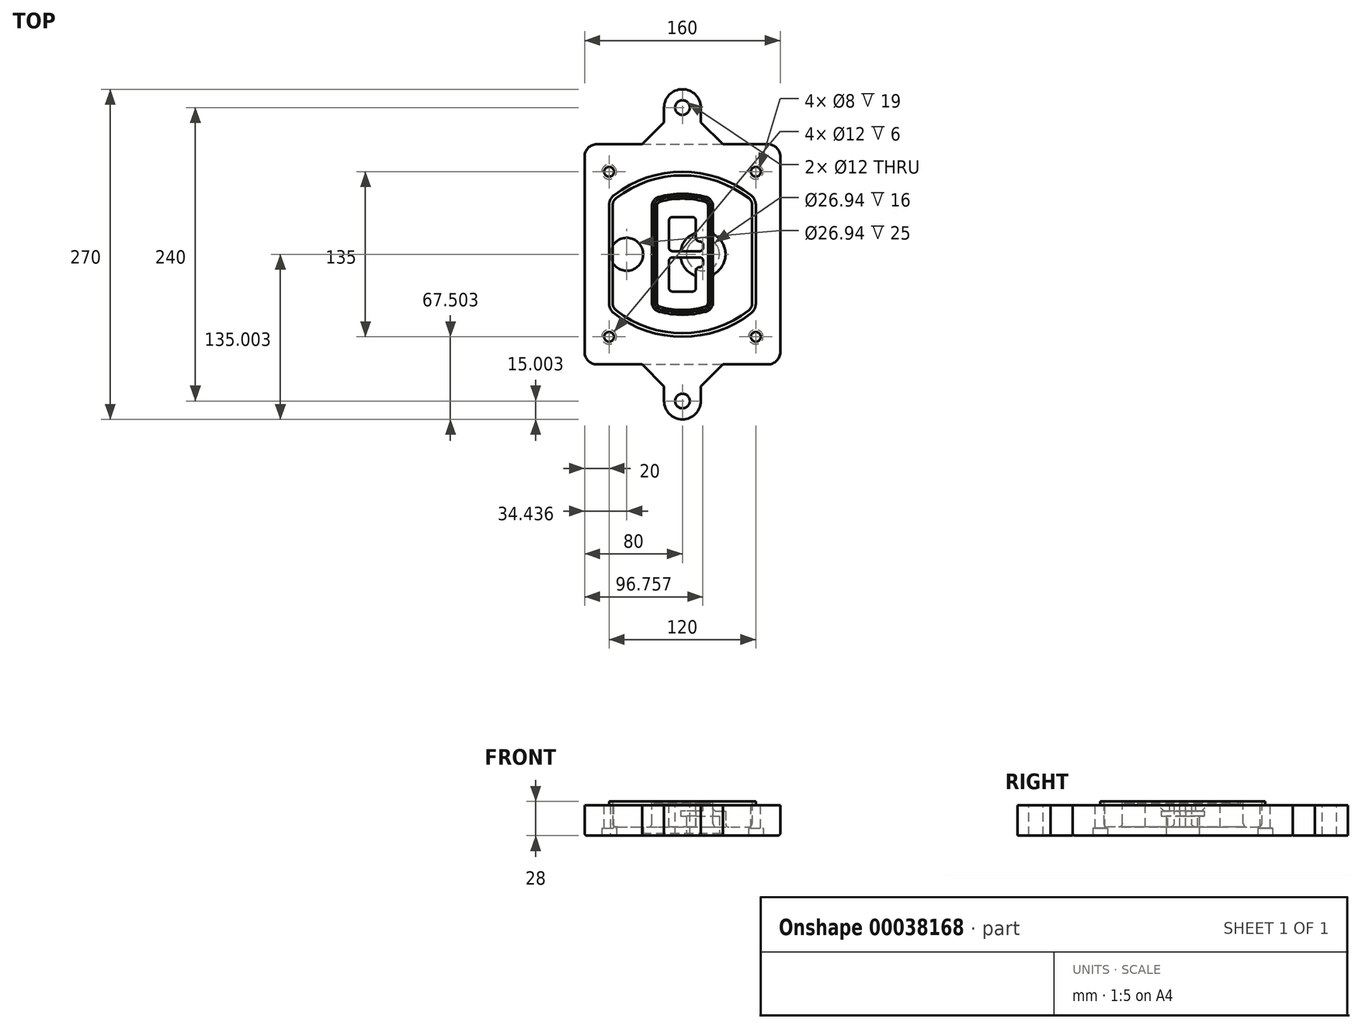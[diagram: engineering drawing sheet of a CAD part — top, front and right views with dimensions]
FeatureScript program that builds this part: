
annotation { "Feature Type Name" : "Feature", "Feature Type Description" : "" }
export const myFeature = defineFeature(function(context is Context, id is Id, definition is map)
    precondition{}
    {
        {
            var Q0;
            Q0=qCreatedBy(makeId("Top.planeOp"),FACE);
            var sketch = newSketch(context, id + "F0", { "sketchPlane" : qUnion([Q0])});
            skPoint(sketch, "E0.rect.middle", {"position": v(0, 0) * mm});
            skLineSegment(sketch, "E1.bottom", {"start": v(24.05, 28.38) * mm, "end": v(164.05, 28.38) * mm});
            skLineSegment(sketch, "E1.top", {"start": v(24.05, 208.38) * mm, "end": v(164.05, 208.38) * mm});
            skLineSegment(sketch, "E1.left", {"start": v(14.05, 38.38) * mm, "end": v(14.05, 198.38) * mm});
            skLineSegment(sketch, "E1.right", {"start": v(174.05, 38.38) * mm, "end": v(174.05, 198.38) * mm});
            skLineSegment(sketch, "E2", {"start": v(14.05, 208.38) * mm, "end": v(174.05, 28.38) * mm, "construction": true});
            skLineSegment(sketch, "E3", {"start": v(174.05, 208.38) * mm, "end": v(14.05, 28.38) * mm, "construction": true});
            skCircle(sketch, "E4", {"center": v(34.05, 185.88) * mm, "radius": 4 * mm});
            skCircle(sketch, "E5", {"center": v(154.05, 185.88) * mm, "radius": 4 * mm});
            skCircle(sketch, "E6", {"center": v(154.05, 50.88) * mm, "radius": 4 * mm});
            skCircle(sketch, "E7", {"center": v(34.05, 50.88) * mm, "radius": 4 * mm});
            skLineSegment(sketch, "E8", {"start": v(34.05, 185.88) * mm, "end": v(154.05, 185.88) * mm, "construction": true});
            skLineSegment(sketch, "E9", {"start": v(154.05, 185.88) * mm, "end": v(154.05, 50.88) * mm, "construction": true});
            skLineSegment(sketch, "E10", {"start": v(154.05, 50.88) * mm, "end": v(34.05, 50.88) * mm, "construction": true});
            skLineSegment(sketch, "E11", {"start": v(34.05, 50.88) * mm, "end": v(34.05, 185.88) * mm, "construction": true});
            skLineSegment(sketch, "E12", {"start": v(34.05, 158.68) * mm, "end": v(34.05, 78.09) * mm});
            skLineSegment(sketch, "E13", {"start": v(154.05, 158.68) * mm, "end": v(154.05, 78.09) * mm});
            skArc(sketch, "E14", {"start": v(150.2, 166.56) * mm, "mid": v(94.05, 185.88) * mm, "end": v(37.9, 166.56) * mm});
            skArc(sketch, "E15", {"start": v(37.9, 70.2) * mm, "mid": v(94.05, 50.88) * mm, "end": v(150.2, 70.2) * mm});
            skLineSegment(sketch, "E16", {"start": v(34.05, 118.38) * mm, "end": v(154.05, 118.38) * mm, "construction": true});
            skPoint(sketch, "E17.visualSharp", {"position": v(34.05, 73.38) * mm});
            skArc(sketch, "E17.filletArc", {"start": v(34.05, 78.09) * mm, "mid": v(35.06, 73.7) * mm, "end": v(37.9, 70.2) * mm});
            skPoint(sketch, "E18.visualSharp", {"position": v(34.05, 163.38) * mm});
            skArc(sketch, "E18.filletArc", {"start": v(37.9, 166.56) * mm, "mid": v(35.06, 163.06) * mm, "end": v(34.05, 158.68) * mm});
            skPoint(sketch, "E19.visualSharp", {"position": v(154.05, 163.38) * mm});
            skArc(sketch, "E19.filletArc", {"start": v(154.05, 158.68) * mm, "mid": v(153.04, 163.06) * mm, "end": v(150.2, 166.56) * mm});
            skPoint(sketch, "E20.visualSharp", {"position": v(154.05, 73.38) * mm});
            skArc(sketch, "E20.filletArc", {"start": v(150.2, 70.2) * mm, "mid": v(153.04, 73.7) * mm, "end": v(154.05, 78.09) * mm});
            skPoint(sketch, "E21.visualSharp", {"position": v(14.05, 208.38) * mm});
            skArc(sketch, "E21.filletArc", {"start": v(24.05, 208.38) * mm, "mid": v(16.98, 205.45) * mm, "end": v(14.05, 198.38) * mm});
            skPoint(sketch, "E22.visualSharp", {"position": v(174.05, 208.38) * mm});
            skArc(sketch, "E22.filletArc", {"start": v(174.05, 198.38) * mm, "mid": v(171.12, 205.45) * mm, "end": v(164.05, 208.38) * mm});
            skPoint(sketch, "E23.visualSharp", {"position": v(174.05, 28.38) * mm});
            skArc(sketch, "E23.filletArc", {"start": v(164.05, 28.38) * mm, "mid": v(171.12, 31.31) * mm, "end": v(174.05, 38.38) * mm});
            skPoint(sketch, "E24.visualSharp", {"position": v(14.05, 28.38) * mm});
            skArc(sketch, "E24.filletArc", {"start": v(14.05, 38.38) * mm, "mid": v(16.98, 31.31) * mm, "end": v(24.05, 28.38) * mm});
            skArc(sketch, "E25.0", {"start": v(151.05, 158.68) * mm, "mid": v(150.34, 161.75) * mm, "end": v(148.36, 164.2) * mm});
            skLineSegment(sketch, "E25.1", {"start": v(151.05, 158.68) * mm, "end": v(151.05, 78.09) * mm});
            skArc(sketch, "E25.2", {"start": v(148.36, 72.57) * mm, "mid": v(150.34, 75.02) * mm, "end": v(151.05, 78.09) * mm});
            skArc(sketch, "E25.3", {"start": v(39.74, 72.57) * mm, "mid": v(94.05, 53.88) * mm, "end": v(148.36, 72.57) * mm});
            skArc(sketch, "E25.4", {"start": v(37.05, 78.09) * mm, "mid": v(37.76, 75.02) * mm, "end": v(39.74, 72.57) * mm});
            skArc(sketch, "E25.5", {"start": v(148.36, 164.2) * mm, "mid": v(94.05, 182.88) * mm, "end": v(39.74, 164.2) * mm});
            skLineSegment(sketch, "E25.6", {"start": v(37.05, 158.68) * mm, "end": v(37.05, 78.09) * mm});
            skArc(sketch, "E25.7", {"start": v(39.74, 164.2) * mm, "mid": v(37.76, 161.75) * mm, "end": v(37.05, 158.68) * mm});
            skArc(sketch, "E26.0", {"start": v(35.43, 169.71) * mm, "mid": v(31.47, 164.82) * mm, "end": v(30.05, 158.68) * mm});
            skArc(sketch, "E26.1", {"start": v(152.67, 169.71) * mm, "mid": v(94.05, 189.88) * mm, "end": v(35.43, 169.71) * mm});
            skArc(sketch, "E26.2", {"start": v(158.05, 158.68) * mm, "mid": v(156.63, 164.82) * mm, "end": v(152.67, 169.71) * mm});
            skLineSegment(sketch, "E26.3", {"start": v(158.05, 158.68) * mm, "end": v(158.05, 78.09) * mm});
            skArc(sketch, "E26.4", {"start": v(152.67, 67.05) * mm, "mid": v(156.63, 71.95) * mm, "end": v(158.05, 78.09) * mm});
            skLineSegment(sketch, "E26.5", {"start": v(30.05, 158.68) * mm, "end": v(30.05, 78.09) * mm});
            skArc(sketch, "E26.6", {"start": v(35.43, 67.05) * mm, "mid": v(94.05, 46.88) * mm, "end": v(152.67, 67.05) * mm});
            skArc(sketch, "E26.7", {"start": v(30.05, 78.09) * mm, "mid": v(31.47, 71.95) * mm, "end": v(35.43, 67.05) * mm});
            skSolve(sketch);
        }
        {
            var Q0;
            Q0=makeQuery(id+"F0.imprint","IMPRINT",FACE,{"disambiguationData":[TD([[makeQuery(id+"F0.imprint","IMPRINT",EDGE,{"derivedFrom":sQuery(id+"F0.wireOp",EDGE,"E1.bottom")}),1.0]])]});
            var Q1;
            Q1=makeQuery(id+"F0.imprint","IMPRINT",FACE,{"disambiguationData":[TD([[makeQuery(id+"F0.imprint","IMPRINT",EDGE,{"derivedFrom":sQuery(id+"F0.wireOp",EDGE,"E12")}),1.0]])]});
            var Q2;
            Q2=makeQuery(id+"F0.imprint","IMPRINT",FACE,{"disambiguationData":[TD([[makeQuery(id+"F0.imprint","IMPRINT",EDGE,{"derivedFrom":sQuery(id+"F0.wireOp",EDGE,"E25.0")}),1.0]])]});
            var Q3;
            Q3=makeQuery(id+"F0.imprint","IMPRINT",FACE,{"disambiguationData":[TD([[makeQuery(id+"F0.imprint","IMPRINT",EDGE,{"derivedFrom":sQuery(id+"F0.wireOp",EDGE,"E12")}),-1.0]])]});
            extrude(context, id + "F1", {"entities" : qUnion([Q0, Q1, Q2, Q3]), "oppositeDirection" : true, "depth" : 25 * mm});
        }
        {
            var Q0;
            Q0=makeQuery(id+"F0.imprint","IMPRINT",FACE,{"disambiguationData":[TD([[makeQuery(id+"F0.imprint","IMPRINT",EDGE,{"derivedFrom":sQuery(id+"F0.wireOp",EDGE,"E12")}),1.0]])]});
            extrude(context, id + "F2", {"entities" : qUnion([Q0]), "operationType" : NewBodyOperationType.ADD, "depth" : 3 * mm});
        }
        {
            var Q0;
            Q0=makeQuery(id+"F0.imprint","IMPRINT",FACE,{"disambiguationData":[TD([[makeQuery(id+"F0.imprint","IMPRINT",EDGE,{"derivedFrom":sQuery(id+"F0.wireOp",EDGE,"E25.0")}),1.0]])]});
            extrude(context, id + "F3", {"entities" : qUnion([Q0]), "operationType" : NewBodyOperationType.REMOVE, "oppositeDirection" : true, "depth" : 18 * mm});
        }
        {
            var Q0;
            Q0=makeQuery(id+"F2.opExtrude","CAP_FACE",FACE,{"disambiguationData":[OSD([sQuery(id+"F0.wireOp",EDGE,"E12"),sQuery(id+"F0.wireOp",EDGE,"E13"),sQuery(id+"F0.wireOp",EDGE,"E14"),sQuery(id+"F0.wireOp",EDGE,"E15"),sQuery(id+"F0.wireOp",EDGE,"E17.filletArc"),sQuery(id+"F0.wireOp",EDGE,"E18.filletArc"),sQuery(id+"F0.wireOp",EDGE,"E19.filletArc"),sQuery(id+"F0.wireOp",EDGE,"E20.filletArc"),sQuery(id+"F0.wireOp",EDGE,"E25.0"),sQuery(id+"F0.wireOp",EDGE,"E25.1"),sQuery(id+"F0.wireOp",EDGE,"E25.2"),sQuery(id+"F0.wireOp",EDGE,"E25.3"),sQuery(id+"F0.wireOp",EDGE,"E25.4"),sQuery(id+"F0.wireOp",EDGE,"E25.5"),sQuery(id+"F0.wireOp",EDGE,"E25.6"),sQuery(id+"F0.wireOp",EDGE,"E25.7")])],"isStart":false});
            var sketch = newSketch(context, id + "F4", { "sketchPlane" : qUnion([Q0])});
            skArc(sketch, "E27.0", {"start": v(74.97, 71.41) * mm, "mid": v(94.05, 68.88) * mm, "end": v(113.13, 71.41) * mm});
            skArc(sketch, "E28.0", {"start": v(113.13, 165.35) * mm, "mid": v(94.05, 167.88) * mm, "end": v(74.97, 165.35) * mm});
            skLineSegment(sketch, "E29", {"start": v(69.05, 157.63) * mm, "end": v(69.05, 79.14) * mm});
            skLineSegment(sketch, "E30", {"start": v(119.05, 157.63) * mm, "end": v(119.05, 79.14) * mm});
            skLineSegment(sketch, "E31", {"start": v(69.05, 163.48) * mm, "end": v(119.05, 163.48) * mm, "construction": true});
            skLineSegment(sketch, "E32", {"start": v(69.05, 73.28) * mm, "end": v(119.05, 73.28) * mm, "construction": true});
            skPoint(sketch, "E33.visualSharp", {"position": v(69.05, 163.48) * mm});
            skArc(sketch, "E33.filletArc", {"start": v(74.97, 165.35) * mm, "mid": v(70.7, 162.5) * mm, "end": v(69.05, 157.63) * mm});
            skPoint(sketch, "E34.visualSharp", {"position": v(119.05, 163.48) * mm});
            skArc(sketch, "E34.filletArc", {"start": v(119.05, 157.63) * mm, "mid": v(117.4, 162.5) * mm, "end": v(113.13, 165.35) * mm});
            skPoint(sketch, "E35.visualSharp", {"position": v(119.05, 73.28) * mm});
            skArc(sketch, "E35.filletArc", {"start": v(113.13, 71.41) * mm, "mid": v(117.4, 74.27) * mm, "end": v(119.05, 79.14) * mm});
            skPoint(sketch, "E36.visualSharp", {"position": v(69.05, 73.28) * mm});
            skArc(sketch, "E36.filletArc", {"start": v(69.05, 79.14) * mm, "mid": v(70.7, 74.27) * mm, "end": v(74.97, 71.41) * mm});
            skArc(sketch, "E37.0", {"start": v(148.36, 164.2) * mm, "mid": v(94.05, 182.88) * mm, "end": v(39.74, 164.2) * mm});
            skArc(sketch, "E37.1", {"start": v(39.74, 164.2) * mm, "mid": v(37.76, 161.75) * mm, "end": v(37.05, 158.68) * mm});
            skLineSegment(sketch, "E37.2", {"start": v(37.05, 158.68) * mm, "end": v(37.05, 78.09) * mm});
            skArc(sketch, "E37.3", {"start": v(37.05, 78.09) * mm, "mid": v(37.76, 75.02) * mm, "end": v(39.74, 72.57) * mm});
            skArc(sketch, "E37.4", {"start": v(39.74, 72.57) * mm, "mid": v(94.05, 53.88) * mm, "end": v(148.36, 72.57) * mm});
            skArc(sketch, "E37.5", {"start": v(148.36, 72.57) * mm, "mid": v(150.34, 75.02) * mm, "end": v(151.05, 78.09) * mm});
            skLineSegment(sketch, "E37.6", {"start": v(151.05, 158.68) * mm, "end": v(151.05, 78.09) * mm});
            skArc(sketch, "E37.7", {"start": v(151.05, 158.68) * mm, "mid": v(150.34, 161.75) * mm, "end": v(148.36, 164.2) * mm});
            skLineSegment(sketch, "E38.0", {"start": v(117.05, 157.63) * mm, "end": v(117.05, 79.14) * mm});
            skArc(sketch, "E38.1", {"start": v(112.61, 73.34) * mm, "mid": v(115.81, 75.49) * mm, "end": v(117.05, 79.14) * mm});
            skArc(sketch, "E38.2", {"start": v(75.49, 73.34) * mm, "mid": v(94.05, 70.88) * mm, "end": v(112.61, 73.34) * mm});
            skArc(sketch, "E38.3", {"start": v(71.05, 79.14) * mm, "mid": v(72.29, 75.49) * mm, "end": v(75.49, 73.34) * mm});
            skLineSegment(sketch, "E38.4", {"start": v(71.05, 157.63) * mm, "end": v(71.05, 79.14) * mm});
            skArc(sketch, "E38.5", {"start": v(117.05, 157.63) * mm, "mid": v(115.81, 161.28) * mm, "end": v(112.61, 163.42) * mm});
            skArc(sketch, "E38.6", {"start": v(75.49, 163.42) * mm, "mid": v(72.29, 161.28) * mm, "end": v(71.05, 157.63) * mm});
            skArc(sketch, "E38.7", {"start": v(112.61, 163.42) * mm, "mid": v(94.05, 165.88) * mm, "end": v(75.49, 163.42) * mm});
            skArc(sketch, "E39.0", {"start": v(115.05, 157.63) * mm, "mid": v(114.23, 160.06) * mm, "end": v(112.1, 161.5) * mm});
            skLineSegment(sketch, "E39.1", {"start": v(115.05, 157.63) * mm, "end": v(115.05, 79.14) * mm});
            skArc(sketch, "E39.2", {"start": v(112.1, 75.27) * mm, "mid": v(114.23, 76.7) * mm, "end": v(115.05, 79.14) * mm});
            skArc(sketch, "E39.3", {"start": v(76, 75.27) * mm, "mid": v(94.05, 72.88) * mm, "end": v(112.1, 75.27) * mm});
            skArc(sketch, "E39.4", {"start": v(73.05, 79.14) * mm, "mid": v(73.87, 76.7) * mm, "end": v(76, 75.27) * mm});
            skArc(sketch, "E39.5", {"start": v(112.1, 161.5) * mm, "mid": v(94.05, 163.88) * mm, "end": v(76, 161.5) * mm});
            skLineSegment(sketch, "E39.6", {"start": v(73.05, 157.63) * mm, "end": v(73.05, 79.14) * mm});
            skArc(sketch, "E39.7", {"start": v(76, 161.5) * mm, "mid": v(73.87, 160.06) * mm, "end": v(73.05, 157.63) * mm});
            skLineSegment(sketch, "E40", {"start": v(69.05, 118.38) * mm, "end": v(119.05, 118.38) * mm, "construction": true});
            skLineSegment(sketch, "E41", {"start": v(83.05, 123.88) * mm, "end": v(83.05, 145.88) * mm});
            skLineSegment(sketch, "E42", {"start": v(86.05, 148.88) * mm, "end": v(102.05, 148.88) * mm});
            skLineSegment(sketch, "E43", {"start": v(105.05, 145.88) * mm, "end": v(105.05, 131.88) * mm});
            skLineSegment(sketch, "E44", {"start": v(108.05, 128.88) * mm, "end": v(108.05, 128.88) * mm});
            skLineSegment(sketch, "E45", {"start": v(111.05, 125.88) * mm, "end": v(111.05, 123.88) * mm});
            skLineSegment(sketch, "E46", {"start": v(108.05, 120.88) * mm, "end": v(86.05, 120.88) * mm});
            skPoint(sketch, "E47.visualSharp", {"position": v(83.05, 148.88) * mm});
            skArc(sketch, "E47.filletArc", {"start": v(86.05, 148.88) * mm, "mid": v(83.93, 148) * mm, "end": v(83.05, 145.88) * mm});
            skPoint(sketch, "E48.visualSharp", {"position": v(105.05, 148.88) * mm});
            skArc(sketch, "E48.filletArc", {"start": v(105.05, 145.88) * mm, "mid": v(104.17, 148) * mm, "end": v(102.05, 148.88) * mm});
            skPoint(sketch, "E49.visualSharp", {"position": v(105.05, 128.88) * mm});
            skArc(sketch, "E49.filletArc", {"start": v(105.05, 131.88) * mm, "mid": v(105.93, 129.76) * mm, "end": v(108.05, 128.88) * mm});
            skPoint(sketch, "E50.visualSharp", {"position": v(111.05, 128.88) * mm});
            skArc(sketch, "E50.filletArc", {"start": v(111.05, 125.88) * mm, "mid": v(110.17, 128) * mm, "end": v(108.05, 128.88) * mm});
            skPoint(sketch, "E51.visualSharp", {"position": v(111.05, 120.88) * mm});
            skArc(sketch, "E51.filletArc", {"start": v(108.05, 120.88) * mm, "mid": v(110.17, 121.76) * mm, "end": v(111.05, 123.88) * mm});
            skPoint(sketch, "E52.visualSharp", {"position": v(83.05, 120.88) * mm});
            skArc(sketch, "E52.filletArc", {"start": v(83.05, 123.88) * mm, "mid": v(83.93, 121.76) * mm, "end": v(86.05, 120.88) * mm});
            skLineSegment(sketch, "E53.0.MirrorCS", {"start": v(108.05, 115.88) * mm, "end": v(86.05, 115.88) * mm});
            skArc(sketch, "E54.0.MirrorCS", {"start": v(83.05, 112.88) * mm, "mid": v(83.93, 115) * mm, "end": v(86.05, 115.88) * mm});
            skLineSegment(sketch, "E55.0.MirrorCS", {"start": v(83.05, 112.88) * mm, "end": v(83.05, 90.88) * mm});
            skArc(sketch, "E56.0.MirrorCS", {"start": v(86.05, 87.88) * mm, "mid": v(83.93, 88.76) * mm, "end": v(83.05, 90.88) * mm});
            skLineSegment(sketch, "E57.0.MirrorCS", {"start": v(86.05, 87.88) * mm, "end": v(102.05, 87.88) * mm});
            skArc(sketch, "E58.0.MirrorCS", {"start": v(105.05, 90.88) * mm, "mid": v(104.17, 88.76) * mm, "end": v(102.05, 87.88) * mm});
            skLineSegment(sketch, "E59.0.MirrorCS", {"start": v(105.05, 90.88) * mm, "end": v(105.05, 104.88) * mm});
            skArc(sketch, "E60.0.MirrorCS", {"start": v(105.05, 104.88) * mm, "mid": v(105.93, 107) * mm, "end": v(108.05, 107.88) * mm});
            skArc(sketch, "E61.0.MirrorCS", {"start": v(111.05, 110.88) * mm, "mid": v(110.17, 108.76) * mm, "end": v(108.05, 107.88) * mm});
            skLineSegment(sketch, "E62.0.MirrorCS", {"start": v(111.05, 110.88) * mm, "end": v(111.05, 112.88) * mm});
            skArc(sketch, "E63.0.MirrorCS", {"start": v(108.05, 115.88) * mm, "mid": v(110.17, 115) * mm, "end": v(111.05, 112.88) * mm});
            skSolve(sketch);
        }
        {
            var Q0;
            Q0=makeQuery(id+"F4.imprint","IMPRINT",FACE,{"disambiguationData":[TD([[makeQuery(id+"F4.imprint","IMPRINT",EDGE,{"derivedFrom":sQuery(id+"F4.wireOp",EDGE,"E27.0")}),1.0]])]});
            var Q1;
            Q1=makeQuery(id+"F4.imprint","IMPRINT",FACE,{"disambiguationData":[TD([[makeQuery(id+"F4.imprint","IMPRINT",EDGE,{"derivedFrom":sQuery(id+"F4.wireOp",EDGE,"E38.0")}),-1.0]])]});
            var Q2;
            Q2=makeQuery(id+"F4.imprint","IMPRINT",FACE,{"disambiguationData":[TD([[makeQuery(id+"F4.imprint","IMPRINT",EDGE,{"derivedFrom":sQuery(id+"F4.wireOp",EDGE,"E39.0")}),1.0]])]});
            extrude(context, id + "F5", {"entities" : qUnion([Q0, Q1, Q2]), "operationType" : NewBodyOperationType.ADD, "endBound" : BoundingType.UP_TO_NEXT, "oppositeDirection" : true, "depth" : 25 * mm});
        }
        {
            var Q0;
            Q0=makeQuery(id+"F4.imprint","IMPRINT",FACE,{"disambiguationData":[TD([[makeQuery(id+"F4.imprint","IMPRINT",EDGE,{"derivedFrom":sQuery(id+"F4.wireOp",EDGE,"E38.0")}),-1.0]])]});
            extrude(context, id + "F6", {"entities" : qUnion([Q0]), "operationType" : NewBodyOperationType.REMOVE, "oppositeDirection" : true, "depth" : 2 * mm});
        }
        {
            var Q0;
            Q0=makeQuery(id+"F1.opExtrude","CAP_FACE",FACE,{"disambiguationData":[OSD([sQuery(id+"F0.wireOp",EDGE,"E1.bottom"),sQuery(id+"F0.wireOp",EDGE,"E1.top"),sQuery(id+"F0.wireOp",EDGE,"E1.left"),sQuery(id+"F0.wireOp",EDGE,"E1.right"),sQuery(id+"F0.wireOp",EDGE,"E4"),sQuery(id+"F0.wireOp",EDGE,"E5"),sQuery(id+"F0.wireOp",EDGE,"E6"),sQuery(id+"F0.wireOp",EDGE,"E7"),sQuery(id+"F0.wireOp",EDGE,"E21.filletArc"),sQuery(id+"F0.wireOp",EDGE,"E22.filletArc"),sQuery(id+"F0.wireOp",EDGE,"E23.filletArc"),sQuery(id+"F0.wireOp",EDGE,"E24.filletArc")])],"isStart":false});
            var sketch = newSketch(context, id + "F7", { "sketchPlane" : qUnion([Q0])});
            skCircle(sketch, "E64", {"center": v(110.8, -118.38) * mm, "radius": 13.47 * mm});
            skCircle(sketch, "E65", {"center": v(48.49, -118.38) * mm, "radius": 13.47 * mm});
            skLineSegment(sketch, "E66", {"start": v(174.05, -118.38) * mm, "end": v(14.05, -118.38) * mm});
            skCircle(sketch, "E67", {"center": v(110.8, -118.38) * mm, "radius": 18.47 * mm});
            skCircle(sketch, "E68", {"center": v(154.05, -185.88) * mm, "radius": 6 * mm});
            skCircle(sketch, "E69", {"center": v(34.05, -185.88) * mm, "radius": 6 * mm});
            skCircle(sketch, "E70", {"center": v(34.05, -50.88) * mm, "radius": 6 * mm});
            skCircle(sketch, "E71", {"center": v(154.05, -50.88) * mm, "radius": 6 * mm});
            skSolve(sketch);
        }
        {
            var Q0;
            {var subQ1=sQuery(id+"F7.wireOp",EDGE,"E66");var subQ4=sQuery(id+"F7.wireOp",EDGE,"E64");var subQ6=makeQuery(id+"F7.imprint","INTERSECT",VERTEX,{"disambiguationData":[OD(0.0)],"derivedFrom":[subQ4,subQ1]});Q0=makeQuery(id+"F7.imprint","IMPRINT",FACE,{"disambiguationData":[TD([[makeQuery(id+"F7.imprint","IMPRINT",EDGE,{"disambiguationData":[TD([[subQ6,-1.0]])],"derivedFrom":subQ4}),-1.0]])]});}
            var Q1;
            {var subQ0=sQuery(id+"F7.wireOp",EDGE,"E66");var subQ1=sQuery(id+"F7.wireOp",EDGE,"E64");var subQ3=makeQuery(id+"F7.imprint","INTERSECT",VERTEX,{"disambiguationData":[OD(0.0)],"derivedFrom":[subQ1,subQ0]});Q1=makeQuery(id+"F7.imprint","IMPRINT",FACE,{"disambiguationData":[TD([[makeQuery(id+"F7.imprint","IMPRINT",EDGE,{"disambiguationData":[TD([[subQ3,-1.0]])],"derivedFrom":subQ1}),1.0]])]});}
            var Q2;
            {var subQ0=sQuery(id+"F7.wireOp",EDGE,"E66");var subQ1=sQuery(id+"F7.wireOp",EDGE,"E64");var subQ3=makeQuery(id+"F7.imprint","INTERSECT",VERTEX,{"disambiguationData":[OD(0.0)],"derivedFrom":[subQ1,subQ0]});Q2=makeQuery(id+"F7.imprint","IMPRINT",FACE,{"disambiguationData":[TD([[makeQuery(id+"F7.imprint","IMPRINT",EDGE,{"disambiguationData":[TD([[subQ3,1.0]])],"derivedFrom":subQ1}),1.0]])]});}
            var Q3;
            {var subQ1=sQuery(id+"F7.wireOp",EDGE,"E66");var subQ4=sQuery(id+"F7.wireOp",EDGE,"E64");var subQ6=makeQuery(id+"F7.imprint","INTERSECT",VERTEX,{"disambiguationData":[OD(0.0)],"derivedFrom":[subQ4,subQ1]});Q3=makeQuery(id+"F7.imprint","IMPRINT",FACE,{"disambiguationData":[TD([[makeQuery(id+"F7.imprint","IMPRINT",EDGE,{"disambiguationData":[TD([[subQ6,1.0]])],"derivedFrom":subQ4}),-1.0]])]});}
            extrude(context, id + "F8", {"entities" : qUnion([Q0, Q1, Q2, Q3]), "operationType" : NewBodyOperationType.ADD, "oppositeDirection" : true, "depth" : 20 * mm});
        }
        {
            var Q0;
            {var subQ0=sQuery(id+"F7.wireOp",EDGE,"E66");var subQ1=sQuery(id+"F7.wireOp",EDGE,"E64");var subQ3=makeQuery(id+"F7.imprint","INTERSECT",VERTEX,{"disambiguationData":[OD(0.0)],"derivedFrom":[subQ1,subQ0]});Q0=makeQuery(id+"F7.imprint","IMPRINT",FACE,{"disambiguationData":[TD([[makeQuery(id+"F7.imprint","IMPRINT",EDGE,{"disambiguationData":[TD([[subQ3,-1.0]])],"derivedFrom":subQ1}),1.0]])]});}
            var Q1;
            {var subQ0=sQuery(id+"F7.wireOp",EDGE,"E66");var subQ1=sQuery(id+"F7.wireOp",EDGE,"E64");var subQ3=makeQuery(id+"F7.imprint","INTERSECT",VERTEX,{"disambiguationData":[OD(0.0)],"derivedFrom":[subQ1,subQ0]});Q1=makeQuery(id+"F7.imprint","IMPRINT",FACE,{"disambiguationData":[TD([[makeQuery(id+"F7.imprint","IMPRINT",EDGE,{"disambiguationData":[TD([[subQ3,1.0]])],"derivedFrom":subQ1}),1.0]])]});}
            extrude(context, id + "F9", {"entities" : qUnion([Q0, Q1]), "operationType" : NewBodyOperationType.REMOVE, "oppositeDirection" : true, "depth" : 16 * mm});
        }
        {
            var Q0;
            {var subQ0=sQuery(id+"F7.wireOp",EDGE,"E66");var subQ1=sQuery(id+"F7.wireOp",EDGE,"E65");var subQ3=makeQuery(id+"F7.imprint","INTERSECT",VERTEX,{"disambiguationData":[OD(0.0)],"derivedFrom":[subQ1,subQ0]});Q0=makeQuery(id+"F7.imprint","IMPRINT",FACE,{"disambiguationData":[TD([[makeQuery(id+"F7.imprint","IMPRINT",EDGE,{"disambiguationData":[TD([[subQ3,-1.0]])],"derivedFrom":subQ1}),1.0]])]});}
            var Q1;
            {var subQ0=sQuery(id+"F7.wireOp",EDGE,"E66");var subQ1=sQuery(id+"F7.wireOp",EDGE,"E65");var subQ3=makeQuery(id+"F7.imprint","INTERSECT",VERTEX,{"disambiguationData":[OD(0.0)],"derivedFrom":[subQ1,subQ0]});Q1=makeQuery(id+"F7.imprint","IMPRINT",FACE,{"disambiguationData":[TD([[makeQuery(id+"F7.imprint","IMPRINT",EDGE,{"disambiguationData":[TD([[subQ3,1.0]])],"derivedFrom":subQ1}),1.0]])]});}
            extrude(context, id + "F10", {"entities" : qUnion([Q0, Q1]), "operationType" : NewBodyOperationType.REMOVE, "oppositeDirection" : true, "depth" : 25 * mm});
        }
        {
            var Q0;
            Q0=makeQuery(id+"F7.imprint","IMPRINT",FACE,{"disambiguationData":[TD([[makeQuery(id+"F7.imprint","IMPRINT",EDGE,{"derivedFrom":sQuery(id+"F7.wireOp",EDGE,"E68")}),1.0]])]});
            var Q1;
            Q1=makeQuery(id+"F7.imprint","IMPRINT",FACE,{"disambiguationData":[TD([[makeQuery(id+"F7.imprint","IMPRINT",EDGE,{"derivedFrom":makeQuery(id+"F1.opExtrude","CAP_EDGE",EDGE,{"disambiguationData":[OSD([sQuery(id+"F0.wireOp",EDGE,"E5")])],"isStart":false})}),-1.0]])]});
            var Q2;
            Q2=makeQuery(id+"F7.imprint","IMPRINT",FACE,{"disambiguationData":[TD([[makeQuery(id+"F7.imprint","IMPRINT",EDGE,{"derivedFrom":sQuery(id+"F7.wireOp",EDGE,"E69")}),1.0]])]});
            var Q3;
            Q3=makeQuery(id+"F7.imprint","IMPRINT",FACE,{"disambiguationData":[TD([[makeQuery(id+"F7.imprint","IMPRINT",EDGE,{"derivedFrom":makeQuery(id+"F1.opExtrude","CAP_EDGE",EDGE,{"disambiguationData":[OSD([sQuery(id+"F0.wireOp",EDGE,"E4")])],"isStart":false})}),-1.0]])]});
            var Q4;
            Q4=makeQuery(id+"F7.imprint","IMPRINT",FACE,{"disambiguationData":[TD([[makeQuery(id+"F7.imprint","IMPRINT",EDGE,{"derivedFrom":sQuery(id+"F7.wireOp",EDGE,"E70")}),1.0]])]});
            var Q5;
            Q5=makeQuery(id+"F7.imprint","IMPRINT",FACE,{"disambiguationData":[TD([[makeQuery(id+"F7.imprint","IMPRINT",EDGE,{"derivedFrom":makeQuery(id+"F1.opExtrude","CAP_EDGE",EDGE,{"disambiguationData":[OSD([sQuery(id+"F0.wireOp",EDGE,"E7")])],"isStart":false})}),-1.0]])]});
            var Q6;
            Q6=makeQuery(id+"F7.imprint","IMPRINT",FACE,{"disambiguationData":[TD([[makeQuery(id+"F7.imprint","IMPRINT",EDGE,{"derivedFrom":sQuery(id+"F7.wireOp",EDGE,"E71")}),1.0]])]});
            var Q7;
            Q7=makeQuery(id+"F7.imprint","IMPRINT",FACE,{"disambiguationData":[TD([[makeQuery(id+"F7.imprint","IMPRINT",EDGE,{"derivedFrom":makeQuery(id+"F1.opExtrude","CAP_EDGE",EDGE,{"disambiguationData":[OSD([sQuery(id+"F0.wireOp",EDGE,"E6")])],"isStart":false})}),-1.0]])]});
            extrude(context, id + "F11", {"entities" : qUnion([Q0, Q1, Q2, Q3, Q4, Q5, Q6, Q7]), "operationType" : NewBodyOperationType.REMOVE, "oppositeDirection" : true, "depth" : 6 * mm});
        }
        {
            var Q0;
            Q0=makeQuery(id+"F9.boolean.opBoolean","COPY",FACE,{"derivedFrom":makeQuery(id+"F9.opExtrude","CAP_FACE",FACE,{"disambiguationData":[OSD([sQuery(id+"F7.wireOp",EDGE,"E64")])],"isStart":false})});
            var sketch = newSketch(context, id + "F12", { "sketchPlane" : qUnion([Q0])});
            skArc(sketch, "E72.0", {"start": v(105.05, -100.83) * mm, "mid": v(96.62, -106.56) * mm, "end": v(92.5, -115.88) * mm});
            skArc(sketch, "E72.1", {"start": v(92.5, -120.88) * mm, "mid": v(96.62, -130.2) * mm, "end": v(105.05, -135.93) * mm});
            skLineSegment(sketch, "E73", {"start": v(92.5, -120.88) * mm, "end": v(108.05, -120.88) * mm});
            skLineSegment(sketch, "E74.0", {"start": v(108.05, -115.88) * mm, "end": v(92.5, -115.88) * mm});
            skArc(sketch, "E74.1", {"start": v(108.05, -115.88) * mm, "mid": v(110.17, -115) * mm, "end": v(111.05, -112.88) * mm});
            skLineSegment(sketch, "E74.2", {"start": v(111.05, -110.88) * mm, "end": v(111.05, -112.88) * mm});
            skArc(sketch, "E74.3", {"start": v(111.05, -110.88) * mm, "mid": v(110.17, -108.76) * mm, "end": v(108.05, -107.88) * mm});
            skArc(sketch, "E74.4", {"start": v(105.05, -104.88) * mm, "mid": v(105.93, -107) * mm, "end": v(108.05, -107.88) * mm});
            skLineSegment(sketch, "E74.5", {"start": v(105.05, -100.83) * mm, "end": v(105.05, -104.88) * mm});
            skLineSegment(sketch, "E74.7", {"start": v(108.05, -120.88) * mm, "end": v(92.5, -120.88) * mm});
            skArc(sketch, "E74.8", {"start": v(108.05, -120.88) * mm, "mid": v(110.17, -121.76) * mm, "end": v(111.05, -123.88) * mm});
            skLineSegment(sketch, "E74.9", {"start": v(111.05, -125.88) * mm, "end": v(111.05, -123.88) * mm});
            skArc(sketch, "E74.10", {"start": v(111.05, -125.88) * mm, "mid": v(110.17, -128) * mm, "end": v(108.05, -128.88) * mm});
            skArc(sketch, "E74.11", {"start": v(105.05, -131.88) * mm, "mid": v(105.93, -129.76) * mm, "end": v(108.05, -128.88) * mm});
            skLineSegment(sketch, "E74.12", {"start": v(105.05, -135.93) * mm, "end": v(105.05, -131.88) * mm});
            skPoint(sketch, "E75.orphan", {"position": v(105.05, -145.88) * mm});
            skPoint(sketch, "E76.orphan", {"position": v(86.05, -120.88) * mm});
            skPoint(sketch, "E77.orphan", {"position": v(86.05, -115.88) * mm});
            skPoint(sketch, "E78.orphan", {"position": v(105.05, -90.88) * mm});
            skSolve(sketch);
        }
        {
            var Q0;
            {var subQ7=sQuery(id+"F12.wireOp",EDGE,"E72.0");var subQ14=sQuery(id+"F12.wireOp",EDGE,"E72.1");var subQ16=sQuery(id+"F12.wireOp",EDGE,"E74.1");var subQ18=sQuery(id+"F12.wireOp",EDGE,"E74.8");Q0=qUnion([makeQuery(id+"F12.imprint","IMPRINT",FACE,{"disambiguationData":[TD([[makeQuery(id+"F12.imprint","IMPRINT",EDGE,{"derivedFrom":subQ7}),1.0]])]}),makeQuery(id+"F12.imprint","IMPRINT",FACE,{"disambiguationData":[TD([[makeQuery(id+"F12.imprint","IMPRINT",EDGE,{"derivedFrom":subQ14}),1.0]])]}),makeQuery(id+"F12.imprint","IMPRINT",FACE,{"disambiguationData":[TD([[makeQuery(id+"F12.imprint","IMPRINT",EDGE,{"derivedFrom":subQ16}),1.0]])]}),makeQuery(id+"F12.imprint","IMPRINT",FACE,{"disambiguationData":[TD([[makeQuery(id+"F12.imprint","IMPRINT",EDGE,{"derivedFrom":subQ18}),-1.0]])]})]);}
            var Q1;
            Q1=makeQuery(id+"F5.boolean.opBoolean","SPLIT",FACE,{"disambiguationData":[TD([makeQuery(id+"F5.opExtrude","SWEPT_FACE",FACE,{"disambiguationData":[OSD([sQuery(id+"F4.wireOp",EDGE,"E41")])]})])],"derivedFrom":makeQuery(id+"F3.boolean.opBoolean","COPY",FACE,{"derivedFrom":makeQuery(id+"F3.opExtrude","CAP_FACE",FACE,{"disambiguationData":[OSD([sQuery(id+"F0.wireOp",EDGE,"E25.0"),sQuery(id+"F0.wireOp",EDGE,"E25.1"),sQuery(id+"F0.wireOp",EDGE,"E25.2"),sQuery(id+"F0.wireOp",EDGE,"E25.3"),sQuery(id+"F0.wireOp",EDGE,"E25.4"),sQuery(id+"F0.wireOp",EDGE,"E25.5"),sQuery(id+"F0.wireOp",EDGE,"E25.6"),sQuery(id+"F0.wireOp",EDGE,"E25.7")])],"isStart":false})})});
            extrude(context, id + "F13", {"entities" : qUnion([Q0]), "operationType" : NewBodyOperationType.REMOVE, "endBound" : BoundingType.UP_TO_SURFACE, "endBoundEntityFace" : qUnion([Q1]), "depth" : 25 * mm});
        }
        {
            var Q0;
            Q0=makeQuery(id+"F3.boolean.opBoolean","COPY",EDGE,{"derivedFrom":makeQuery(id+"F3.opExtrude","CAP_EDGE",EDGE,{"disambiguationData":[OSD([sQuery(id+"F0.wireOp",EDGE,"E25.6")])],"isStart":false})});
            var Q1;
            Q1=makeQuery(id+"F8.boolean.opBoolean","INTERSECT",EDGE,{"derivedFrom":[makeQuery(id+"F5.opExtrude","SWEPT_FACE",FACE,{"disambiguationData":[OSD([sQuery(id+"F4.wireOp",EDGE,"E30")])]}),makeQuery(id+"F8.opExtrude","CAP_FACE",FACE,{"disambiguationData":[OSD([sQuery(id+"F7.wireOp",EDGE,"E67")])],"isStart":false})]});
            var Q2;
            Q2=makeQuery(id+"F8.boolean.opBoolean","INTERSECT",EDGE,{"disambiguationData":[OD(1.0)],"derivedFrom":[makeQuery(id+"F5.opExtrude","SWEPT_FACE",FACE,{"disambiguationData":[OSD([sQuery(id+"F4.wireOp",EDGE,"E30")])]}),makeQuery(id+"F8.opExtrude","SWEPT_FACE",FACE,{"disambiguationData":[OSD([sQuery(id+"F7.wireOp",EDGE,"E67")])]})]});
            var Q3;
            {var subQ0=sQuery(id+"F4.wireOp",EDGE,"E30");Q3=makeQuery(id+"F8.boolean.opBoolean","SPLIT",EDGE,{"disambiguationData":[TD([makeQuery(id+"F5.opExtrude","SWEPT_FACE",FACE,{"disambiguationData":[OSD([sQuery(id+"F4.wireOp",EDGE,"E35.filletArc")])]})])],"derivedFrom":makeQuery(id+"F5.opExtrude","CAP_EDGE",EDGE,{"disambiguationData":[OSD([subQ0])],"isStart":false})});}
            var Q4;
            {var subQ0=sQuery(id+"F0.wireOp",EDGE,"E25.7");var subQ1=sQuery(id+"F0.wireOp",EDGE,"E25.1");var subQ2=sQuery(id+"F0.wireOp",EDGE,"E25.6");var subQ3=sQuery(id+"F0.wireOp",EDGE,"E25.5");var subQ4=sQuery(id+"F0.wireOp",EDGE,"E25.4");var subQ5=sQuery(id+"F0.wireOp",EDGE,"E25.0");var subQ6=sQuery(id+"F0.wireOp",EDGE,"E25.2");var subQ7=sQuery(id+"F0.wireOp",EDGE,"E25.3");Q4=makeQuery(id+"F8.boolean.opBoolean","INTERSECT",EDGE,{"derivedFrom":[makeQuery(id+"F5.boolean.opBoolean","SPLIT",FACE,{"disambiguationData":[TD([makeQuery(id+"F2.opExtrude","SWEPT_FACE",FACE,{"disambiguationData":[OSD([subQ5])]})])],"derivedFrom":makeQuery(id+"F3.boolean.opBoolean","COPY",FACE,{"derivedFrom":makeQuery(id+"F3.opExtrude","CAP_FACE",FACE,{"disambiguationData":[OSD([subQ5,subQ1,subQ6,subQ7,subQ4,subQ3,subQ2,subQ0])],"isStart":false})})}),makeQuery(id+"F8.opExtrude","SWEPT_FACE",FACE,{"disambiguationData":[OSD([sQuery(id+"F7.wireOp",EDGE,"E67")])]})]});}
            var Q5;
            Q5=makeQuery(id+"F8.boolean.opBoolean","INTERSECT",EDGE,{"disambiguationData":[OD(0.0)],"derivedFrom":[makeQuery(id+"F5.opExtrude","SWEPT_FACE",FACE,{"disambiguationData":[OSD([sQuery(id+"F4.wireOp",EDGE,"E30")])]}),makeQuery(id+"F8.opExtrude","SWEPT_FACE",FACE,{"disambiguationData":[OSD([sQuery(id+"F7.wireOp",EDGE,"E67")])]})]});
            fillet(context, id + "F14", {"entities" : qUnion([Q0, Q1, Q2, Q3, Q4, Q5]), "radius" : 3 * mm, "tangentPropagation" : true, "allowEdgeOverflow" : false});
        }
        {
            var Q0;
            Q0=makeQuery(id+"F1.opExtrude","CAP_EDGE",EDGE,{"disambiguationData":[OSD([sQuery(id+"F0.wireOp",EDGE,"E1.bottom")])],"isStart":false});
            fillet(context, id + "F15", {"entities" : qUnion([Q0]), "radius" : 2 * mm, "tangentPropagation" : true, "allowEdgeOverflow" : false});
        }
        {
            var Q0;
            {var subQ0=sQuery(id+"F0.wireOp",EDGE,"E1.bottom");var subQ1=sQuery(id+"F0.wireOp",EDGE,"E1.top");var subQ2=sQuery(id+"F0.wireOp",EDGE,"E1.left");var subQ3=sQuery(id+"F0.wireOp",EDGE,"E1.right");var subQ4=sQuery(id+"F0.wireOp",EDGE,"E4");var subQ5=sQuery(id+"F0.wireOp",EDGE,"E5");var subQ6=sQuery(id+"F0.wireOp",EDGE,"E6");var subQ7=sQuery(id+"F0.wireOp",EDGE,"E7");var subQ8=sQuery(id+"F0.wireOp",EDGE,"E21.filletArc");var subQ9=sQuery(id+"F0.wireOp",EDGE,"E22.filletArc");var subQ10=sQuery(id+"F0.wireOp",EDGE,"E23.filletArc");var subQ11=sQuery(id+"F0.wireOp",EDGE,"E24.filletArc");Q0=makeQuery(id+"F2.boolean.opBoolean","SPLIT",FACE,{"disambiguationData":[TD([makeQuery(id+"F1.opExtrude","SWEPT_FACE",FACE,{"disambiguationData":[OSD([subQ0])]})])],"derivedFrom":makeQuery(id+"F1.opExtrude","CAP_FACE",FACE,{"disambiguationData":[OSD([subQ0,subQ1,subQ2,subQ3,subQ4,subQ5,subQ6,subQ7,subQ8,subQ9,subQ10,subQ11])],"isStart":true})});}
            var sketch = newSketch(context, id + "F16", { "sketchPlane" : qUnion([Q0])});
            skArc(sketch, "E79.0", {"start": v(37.9, 166.56) * mm, "mid": v(35.06, 163.06) * mm, "end": v(34.05, 158.68) * mm});
            skLineSegment(sketch, "E79.1", {"start": v(34.05, 158.68) * mm, "end": v(34.05, 78.09) * mm});
            skArc(sketch, "E79.2", {"start": v(150.2, 166.56) * mm, "mid": v(94.05, 185.88) * mm, "end": v(37.9, 166.56) * mm});
            skArc(sketch, "E79.3", {"start": v(154.05, 158.68) * mm, "mid": v(153.04, 163.06) * mm, "end": v(150.2, 166.56) * mm});
            skLineSegment(sketch, "E79.4", {"start": v(154.05, 158.68) * mm, "end": v(154.05, 78.09) * mm});
            skArc(sketch, "E79.5", {"start": v(150.2, 70.2) * mm, "mid": v(153.04, 73.7) * mm, "end": v(154.05, 78.09) * mm});
            skArc(sketch, "E79.6", {"start": v(37.9, 70.2) * mm, "mid": v(94.05, 50.88) * mm, "end": v(150.2, 70.2) * mm});
            skArc(sketch, "E79.7", {"start": v(34.05, 78.09) * mm, "mid": v(35.06, 73.7) * mm, "end": v(37.9, 70.2) * mm});
            skCircle(sketch, "E79.8", {"center": v(34.05, 50.88) * mm, "radius": 4 * mm});
            skCircle(sketch, "E79.9", {"center": v(154.05, 185.88) * mm, "radius": 4 * mm});
            skCircle(sketch, "E79.10", {"center": v(154.05, 50.88) * mm, "radius": 4 * mm});
            skCircle(sketch, "E79.11", {"center": v(34.05, 185.88) * mm, "radius": 4 * mm});
            skArc(sketch, "E80.12", {"start": v(24.05, 208.38) * mm, "mid": v(16.98, 205.45) * mm, "end": v(14.05, 198.38) * mm});
            skLineSegment(sketch, "E80.13", {"start": v(14.05, 38.38) * mm, "end": v(14.05, 198.38) * mm});
            skLineSegment(sketch, "E80.14", {"start": v(24.05, 28.38) * mm, "end": v(164.05, 28.38) * mm});
            skArc(sketch, "E80.15", {"start": v(14.05, 38.38) * mm, "mid": v(16.98, 31.31) * mm, "end": v(24.05, 28.38) * mm});
            skArc(sketch, "E80.16", {"start": v(164.05, 28.38) * mm, "mid": v(171.12, 31.31) * mm, "end": v(174.05, 38.38) * mm});
            skLineSegment(sketch, "E80.17", {"start": v(174.05, 38.38) * mm, "end": v(174.05, 198.38) * mm});
            skArc(sketch, "E80.18", {"start": v(174.05, 198.38) * mm, "mid": v(171.12, 205.45) * mm, "end": v(164.05, 208.38) * mm});
            skLineSegment(sketch, "E80.19", {"start": v(24.05, 208.38) * mm, "end": v(164.05, 208.38) * mm});
            skCircle(sketch, "E81", {"center": v(94.05, 238.38) * mm, "radius": 6 * mm});
            skArc(sketch, "E82", {"start": v(109.05, 238.38) * mm, "mid": v(94.05, 253.38) * mm, "end": v(79.05, 238.38) * mm});
            skLineSegment(sketch, "E83", {"start": v(79.05, 238.38) * mm, "end": v(79.05, 226.38) * mm});
            skLineSegment(sketch, "E84", {"start": v(79.05, 226.38) * mm, "end": v(61.05, 208.38) * mm});
            skLineSegment(sketch, "E85", {"start": v(109.05, 238.38) * mm, "end": v(109.05, 226.38) * mm});
            skLineSegment(sketch, "E86", {"start": v(109.05, 226.38) * mm, "end": v(127.05, 208.38) * mm});
            skLineSegment(sketch, "E87", {"start": v(94.05, 238.38) * mm, "end": v(94.05, 208.38) * mm, "construction": true});
            skArc(sketch, "E88.MirrorCS", {"start": v(79.05, 238.38) * mm, "mid": v(94.05, 253.38) * mm, "end": v(109.05, 238.38) * mm});
            skLineSegment(sketch, "E89", {"start": v(174.05, 118.38) * mm, "end": v(14.05, 118.38) * mm, "construction": true});
            skLineSegment(sketch, "E90.MirrorCS", {"start": v(109.05, 10.38) * mm, "end": v(127.05, 28.38) * mm});
            skLineSegment(sketch, "E91.MirrorCS", {"start": v(79.05, 10.38) * mm, "end": v(61.05, 28.38) * mm});
            skLineSegment(sketch, "E92.MirrorCS", {"start": v(79.05, -1.62) * mm, "end": v(79.05, 10.38) * mm});
            skArc(sketch, "E93.MirrorCS", {"start": v(109.05, -1.62) * mm, "mid": v(94.05, -16.62) * mm, "end": v(79.05, -1.62) * mm});
            skLineSegment(sketch, "E94.MirrorCS", {"start": v(109.05, -1.62) * mm, "end": v(109.05, 10.38) * mm});
            skCircle(sketch, "E95.MirrorC", {"center": v(94.05, -1.62) * mm, "radius": 6 * mm});
            skLineSegment(sketch, "E96.MirrorCS", {"start": v(94.05, -1.62) * mm, "end": v(94.05, 28.38) * mm});
            skSolve(sketch);
        }
        {
            var Q0;
            {var subQ2=sQuery(id+"F16.wireOp",EDGE,"E84");Q0=makeQuery(id+"F16.imprint","IMPRINT",FACE,{"disambiguationData":[TD([[makeQuery(id+"F16.imprint","IMPRINT",EDGE,{"derivedFrom":subQ2}),1.0]])]});}
            var Q1;
            {var subQ3=sQuery(id+"F16.wireOp",EDGE,"E90.MirrorCS");Q1=makeQuery(id+"F16.imprint","IMPRINT",FACE,{"disambiguationData":[TD([[makeQuery(id+"F16.imprint","IMPRINT",EDGE,{"derivedFrom":subQ3}),1.0]])]});}
            var Q2;
            Q2=makeQuery(id+"F1.opExtrude","CAP_FACE",FACE,{"disambiguationData":[OSD([sQuery(id+"F0.wireOp",EDGE,"E1.bottom"),sQuery(id+"F0.wireOp",EDGE,"E1.top"),sQuery(id+"F0.wireOp",EDGE,"E1.left"),sQuery(id+"F0.wireOp",EDGE,"E1.right"),sQuery(id+"F0.wireOp",EDGE,"E4"),sQuery(id+"F0.wireOp",EDGE,"E5"),sQuery(id+"F0.wireOp",EDGE,"E6"),sQuery(id+"F0.wireOp",EDGE,"E7"),sQuery(id+"F0.wireOp",EDGE,"E21.filletArc"),sQuery(id+"F0.wireOp",EDGE,"E22.filletArc"),sQuery(id+"F0.wireOp",EDGE,"E23.filletArc"),sQuery(id+"F0.wireOp",EDGE,"E24.filletArc")])],"isStart":false});
            extrude(context, id + "F17", {"entities" : qUnion([Q0, Q1]), "operationType" : NewBodyOperationType.ADD, "endBound" : BoundingType.UP_TO_SURFACE, "oppositeDirection" : true, "endBoundEntityFace" : qUnion([Q2]), "depth" : 25 * mm});
        }
    });
